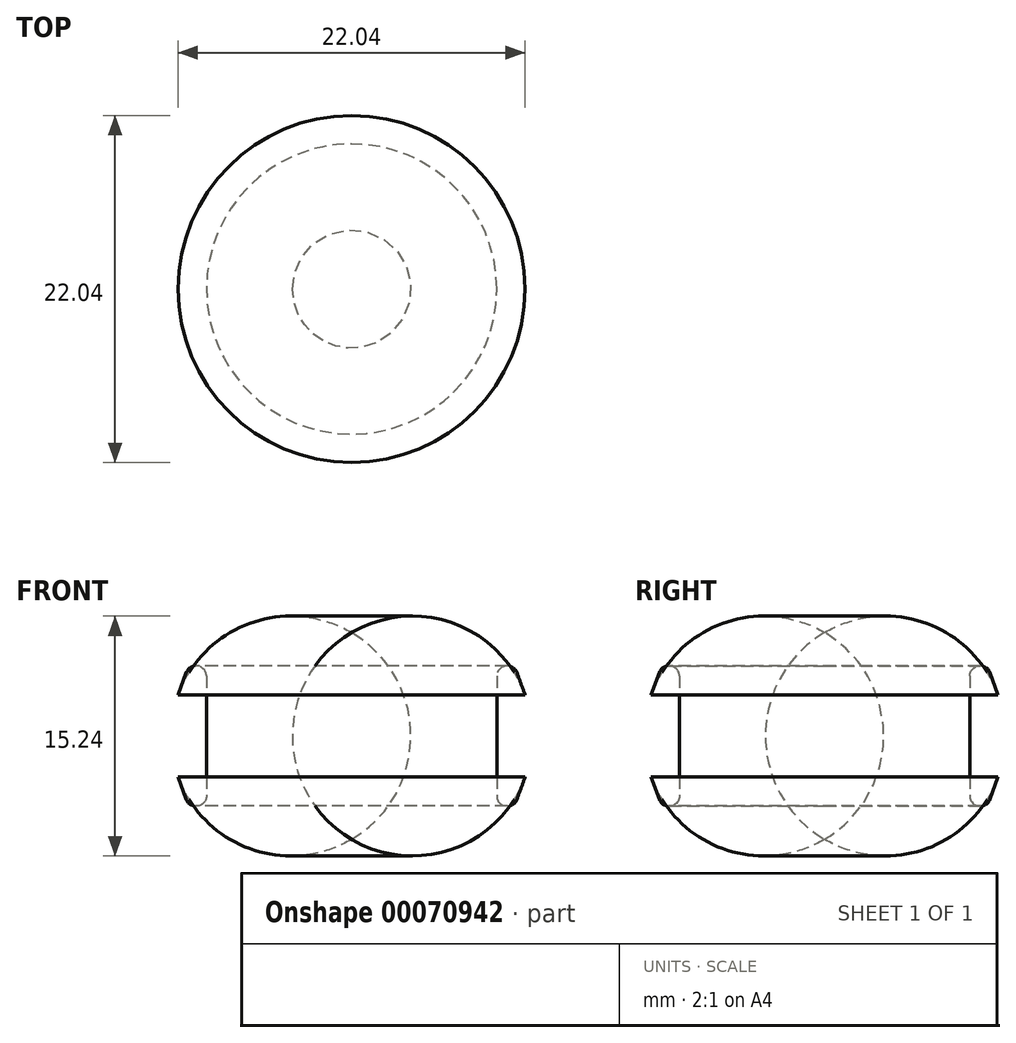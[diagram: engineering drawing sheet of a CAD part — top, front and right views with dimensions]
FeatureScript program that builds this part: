
annotation { "Feature Type Name" : "Feature", "Feature Type Description" : "" }
export const myFeature = defineFeature(function(context is Context, id is Id, definition is map)
    precondition{}
    {
        {
            var Q0;
            Q0=qCreatedBy(makeId("Top.planeOp"),FACE);
            var sketch = newSketch(context, id + "F0", { "sketchPlane" : qUnion([Q0])});
            skCircle(sketch, "E0", {"center": v(0, 0) * mm, "radius": 11.75 * mm});
            skCircle(sketch, "E1", {"center": v(0, 0) * mm, "radius": 9.53 * mm});
            skPoint(sketch, "E2", {"position": v(11.75, 0) * mm});
            skSolve(sketch);
        }
        {
            var Q0;
            Q0=qCreatedBy(makeId("Front.planeOp"),FACE);
            var sketch = newSketch(context, id + "F1", { "sketchPlane" : qUnion([Q0])});
            skLineSegment(sketch, "E3.rect.bottom", {"start": v(13.03, 4.45) * mm, "end": v(9.22, 4.45) * mm});
            skLineSegment(sketch, "E3.rect.top", {"start": v(13.03, -4.44) * mm, "end": v(9.22, -4.44) * mm});
            skLineSegment(sketch, "E3.rect.left", {"start": v(11.97, 6.6) * mm, "end": v(11.97, -4.44) * mm});
            skLineSegment(sketch, "E3.rect.right", {"start": v(9.22, 4.45) * mm, "end": v(9.22, -4.44) * mm});
            skPoint(sketch, "E3.rect.middle", {"position": v(11.12, 0) * mm});
            skSolve(sketch);
        }
        {
            var Q0;
            {var subQ2=sQuery(id+"F1.wireOp",EDGE,"E3.rect.left");Q0=makeQuery(id+"F1.imprint","IMPRINT",FACE,{"disambiguationData":[TD([[makeQuery(id+"F1.imprint","IMPRINT",EDGE,{"derivedFrom":subQ2}),-1.0]])]});}
            var Q1;
            Q1=sQuery(id+"F0.wireOp",EDGE,"E1");
            revolve(context, id + "F2", {"entities" : qUnion([Q0]), "axis" : qUnion([Q1]), "revolveType" : RevolveType.FULL});
        }
        {
            var Q0;
            Q0=makeQuery(id+"F2.opRevolve","SWEPT_EDGE",EDGE,{"disambiguationData":[OSD([sQuery(id+"F1.wireOp",EDGE,"E3.rect.bottom"),sQuery(id+"F1.wireOp",EDGE,"E3.rect.left")])]});
            var Q1;
            Q1=makeQuery(id+"F2.opRevolve","SWEPT_EDGE",EDGE,{"disambiguationData":[OSD([sQuery(id+"F1.wireOp",EDGE,"E3.rect.top"),sQuery(id+"F1.wireOp",EDGE,"E3.rect.left")])]});
            chamfer(context, id + "F3", {"entities" : qUnion([Q0, Q1]), "chamferType" : ChamferType.OFFSET_ANGLE, "width" : 4.44 * mm, "oppositeDirection" : false, "angle" : 20 * degree, "tangentPropagation" : true});
        }
        {
            var Q0;
            Q0=makeQuery(id+"F2.opRevolve","SWEPT_EDGE",EDGE,{"disambiguationData":[OSD([sQuery(id+"F1.wireOp",EDGE,"E3.rect.bottom"),sQuery(id+"F1.wireOp",EDGE,"E3.rect.right")])]});
            var Q1;
            {var subQ0=sQuery(id+"F1.wireOp",EDGE,"E3.rect.bottom");Q1=makeQuery(id+"F3.opChamfer","BLEND_EDGE",EDGE,{"blendedFrom":[makeQuery(id+"F2.opRevolve","SWEPT_EDGE",EDGE,{"disambiguationData":[OSD([subQ0,sQuery(id+"F1.wireOp",EDGE,"E3.rect.left")])]}),makeQuery(id+"F2.opRevolve","SWEPT_FACE",FACE,{"disambiguationData":[OSD([subQ0])]})],"blendedInto":[makeQuery(id+"F2.opRevolve","SWEPT_FACE",FACE,{"disambiguationData":[OSD([subQ0])]})]});}
            var Q2;
            {var subQ0=sQuery(id+"F1.wireOp",EDGE,"E3.rect.top");Q2=makeQuery(id+"F3.opChamfer","BLEND_EDGE",EDGE,{"blendedFrom":[makeQuery(id+"F2.opRevolve","SWEPT_EDGE",EDGE,{"disambiguationData":[OSD([subQ0,sQuery(id+"F1.wireOp",EDGE,"E3.rect.left")])]}),makeQuery(id+"F2.opRevolve","SWEPT_FACE",FACE,{"disambiguationData":[OSD([subQ0])]})],"blendedInto":[makeQuery(id+"F2.opRevolve","SWEPT_FACE",FACE,{"disambiguationData":[OSD([subQ0])]})]});}
            var Q3;
            Q3=makeQuery(id+"F2.opRevolve","SWEPT_EDGE",EDGE,{"disambiguationData":[OSD([sQuery(id+"F1.wireOp",EDGE,"E3.rect.top"),sQuery(id+"F1.wireOp",EDGE,"E3.rect.right")])]});
            fillet(context, id + "F4", {"entities" : qUnion([Q0, Q1, Q2, Q3]), "radius" : 0.64 * mm, "tangentPropagation" : true, "allowEdgeOverflow" : false});
        }
        {
            var Q0;
            {var subQ0=sQuery(id+"F1.wireOp",EDGE,"E3.rect.left");Q0=makeQuery(id+"F3.opChamfer","BLEND_EDGE",EDGE,{"blendedFrom":[makeQuery(id+"F2.opRevolve","SWEPT_EDGE",EDGE,{"disambiguationData":[OSD([sQuery(id+"F1.wireOp",EDGE,"E3.rect.top"),subQ0])]}),makeQuery(id+"F2.opRevolve","SWEPT_EDGE",EDGE,{"disambiguationData":[OSD([sQuery(id+"F1.wireOp",EDGE,"E3.rect.bottom"),subQ0])]})],"blendedInto":[]});}
            fillet(context, id + "F5", {"entities" : qUnion([Q0]), "radius" : 7.62 * mm, "tangentPropagation" : true, "allowEdgeOverflow" : false});
        }
    });
